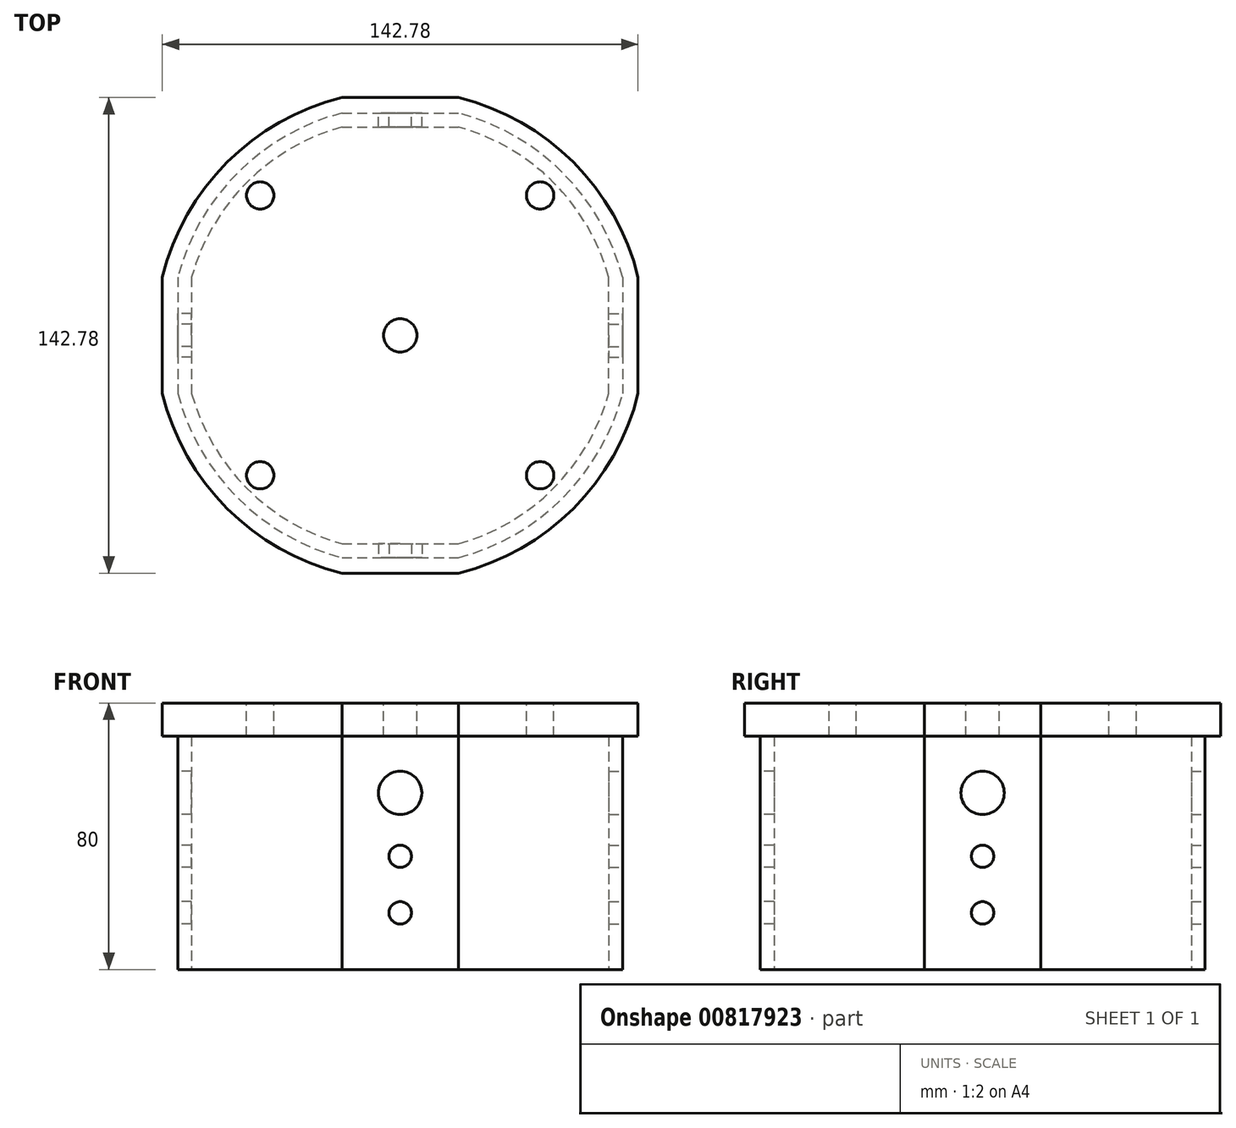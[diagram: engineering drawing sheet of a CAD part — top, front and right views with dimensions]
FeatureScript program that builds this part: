
annotation { "Feature Type Name" : "Feature", "Feature Type Description" : "" }
export const myFeature = defineFeature(function(context is Context, id is Id, definition is map)
    precondition{}
    {
        {
            var Q0;
            Q0=qCreatedBy(makeId("Top.planeOp"),FACE);
            var sketch = newSketch(context, id + "F0", { "sketchPlane" : qUnion([Q0])});
            skArc(sketch, "E0", {"start": v(-17.5, 66.74) * mm, "mid": v(-48.8, 48.8) * mm, "end": v(-66.74, 17.5) * mm});
            skArc(sketch, "E1", {"start": v(-66.74, -17.5) * mm, "mid": v(-48.8, -48.8) * mm, "end": v(-17.5, -66.74) * mm});
            skArc(sketch, "E2", {"start": v(17.5, -66.74) * mm, "mid": v(48.8, -48.8) * mm, "end": v(66.74, -17.5) * mm});
            skArc(sketch, "E3", {"start": v(66.74, 17.5) * mm, "mid": v(48.8, 48.8) * mm, "end": v(17.5, 66.74) * mm});
            skLineSegment(sketch, "E4", {"start": v(-66.74, 17.5) * mm, "end": v(-66.74, -17.5) * mm});
            skLineSegment(sketch, "E5", {"start": v(-17.5, 66.74) * mm, "end": v(17.5, 66.74) * mm});
            skLineSegment(sketch, "E6", {"start": v(66.74, 17.5) * mm, "end": v(66.74, -17.5) * mm});
            skLineSegment(sketch, "E7", {"start": v(-17.5, -66.74) * mm, "end": v(17.5, -66.74) * mm});
            skArc(sketch, "E8", {"start": v(-17.5, 62.6) * mm, "mid": v(-45.96, 45.96) * mm, "end": v(-62.6, 17.5) * mm});
            skArc(sketch, "E9", {"start": v(-62.6, -17.5) * mm, "mid": v(-45.96, -45.96) * mm, "end": v(-17.5, -62.6) * mm});
            skArc(sketch, "E10", {"start": v(17.5, -62.6) * mm, "mid": v(45.96, -45.96) * mm, "end": v(62.6, -17.5) * mm});
            skArc(sketch, "E11", {"start": v(62.6, 17.5) * mm, "mid": v(45.96, 45.96) * mm, "end": v(17.5, 62.6) * mm});
            skLineSegment(sketch, "E12", {"start": v(-17.5, 62.6) * mm, "end": v(17.5, 62.6) * mm});
            skLineSegment(sketch, "E13", {"start": v(-62.6, 17.5) * mm, "end": v(-62.6, -17.5) * mm});
            skLineSegment(sketch, "E14", {"start": v(-17.5, -62.6) * mm, "end": v(17.5, -62.6) * mm});
            skLineSegment(sketch, "E15", {"start": v(62.6, -17.5) * mm, "end": v(62.6, 17.5) * mm});
            skSolve(sketch);
        }
        {
            var Q0;
            Q0 = qSketchRegion(id + "F0", true);
            extrude(context, id + "F1", {"entities" : qUnion([Q0]), "depth" : 70 * mm, "offsetDistance" : 25 * mm});
        }
        {
            var Q0;
            Q0=makeQuery(id+"F1.opExtrude","CAP_FACE",FACE,{"disambiguationData":[OSD([sQuery(id+"F0.wireOp",EDGE,"E0"),sQuery(id+"F0.wireOp",EDGE,"E1"),sQuery(id+"F0.wireOp",EDGE,"E2"),sQuery(id+"F0.wireOp",EDGE,"E3"),sQuery(id+"F0.wireOp",EDGE,"E4"),sQuery(id+"F0.wireOp",EDGE,"E5"),sQuery(id+"F0.wireOp",EDGE,"E6"),sQuery(id+"F0.wireOp",EDGE,"E7"),sQuery(id+"F0.wireOp",EDGE,"E8"),sQuery(id+"F0.wireOp",EDGE,"E9"),sQuery(id+"F0.wireOp",EDGE,"E10"),sQuery(id+"F0.wireOp",EDGE,"E11"),sQuery(id+"F0.wireOp",EDGE,"E12"),sQuery(id+"F0.wireOp",EDGE,"E13"),sQuery(id+"F0.wireOp",EDGE,"E14"),sQuery(id+"F0.wireOp",EDGE,"E15")])],"isStart":false});
            var sketch = newSketch(context, id + "F2", { "sketchPlane" : qUnion([Q0])});
            skArc(sketch, "E16", {"start": v(-17.5, 71.39) * mm, "mid": v(-51.97, 51.97) * mm, "end": v(-71.39, 17.5) * mm});
            skArc(sketch, "E17", {"start": v(-71.39, -17.5) * mm, "mid": v(-51.97, -51.97) * mm, "end": v(-17.5, -71.39) * mm});
            skArc(sketch, "E18", {"start": v(17.5, -71.39) * mm, "mid": v(51.97, -51.97) * mm, "end": v(71.39, -17.5) * mm});
            skArc(sketch, "E19", {"start": v(71.39, 17.5) * mm, "mid": v(51.97, 51.97) * mm, "end": v(17.5, 71.39) * mm});
            skLineSegment(sketch, "E20", {"start": v(-71.39, 17.5) * mm, "end": v(-71.39, -17.5) * mm});
            skLineSegment(sketch, "E21", {"start": v(-17.5, 71.39) * mm, "end": v(17.5, 71.39) * mm});
            skLineSegment(sketch, "E22", {"start": v(71.39, 17.5) * mm, "end": v(71.39, -17.5) * mm});
            skLineSegment(sketch, "E23", {"start": v(-17.5, -71.39) * mm, "end": v(17.5, -71.39) * mm});
            skSolve(sketch);
        }
        {
            var Q0;
            Q0 = qSketchRegion(id + "F2", true);
            extrude(context, id + "F3", {"entities" : qUnion([Q0]), "operationType" : NewBodyOperationType.ADD, "depth" : 10 * mm, "offsetDistance" : 25 * mm});
        }
        {
            var Q0;
            Q0=makeQuery(id+"F1.opExtrude","SWEPT_FACE",FACE,{"disambiguationData":[OSD([sQuery(id+"F0.wireOp",EDGE,"E7")])]});
            var sketch = newSketch(context, id + "F4", { "sketchPlane" : qUnion([Q0])});
            skCircle(sketch, "E24", {"center": v(0, 53) * mm, "radius": 6.5 * mm});
            skCircle(sketch, "E25", {"center": v(0, 34) * mm, "radius": 3.35 * mm});
            skCircle(sketch, "E26", {"center": v(0, 17) * mm, "radius": 3.35 * mm});
            skSolve(sketch);
        }
        {
            var Q0;
            Q0 = qSketchRegion(id + "F4", true);
            extrude(context, id + "F5", {"entities" : qUnion([Q0]), "operationType" : NewBodyOperationType.REMOVE, "endBound" : BoundingType.UP_TO_NEXT, "oppositeDirection" : true, "depth" : 25 * mm, "offsetDistance" : 25 * mm});
        }
        {
            var Q0;
            Q0=makeQuery(id+"F1.opExtrude","SWEPT_FACE",FACE,{"disambiguationData":[OSD([sQuery(id+"F0.wireOp",EDGE,"E6")])]});
            var sketch = newSketch(context, id + "F6", { "sketchPlane" : qUnion([Q0])});
            skCircle(sketch, "E27", {"center": v(0, 53) * mm, "radius": 6.5 * mm});
            skCircle(sketch, "E28", {"center": v(0, 34) * mm, "radius": 3.35 * mm});
            skCircle(sketch, "E29", {"center": v(0, 17) * mm, "radius": 3.35 * mm});
            skSolve(sketch);
        }
        {
            var Q0;
            Q0 = qSketchRegion(id + "F6", true);
            extrude(context, id + "F7", {"entities" : qUnion([Q0]), "operationType" : NewBodyOperationType.REMOVE, "endBound" : BoundingType.UP_TO_NEXT, "oppositeDirection" : true, "depth" : 25 * mm, "offsetDistance" : 25 * mm});
        }
        {
            var Q0;
            Q0=makeQuery(id+"F1.opExtrude","SWEPT_FACE",FACE,{"disambiguationData":[OSD([sQuery(id+"F0.wireOp",EDGE,"E5")])]});
            var sketch = newSketch(context, id + "F8", { "sketchPlane" : qUnion([Q0])});
            skCircle(sketch, "E30", {"center": v(0, 53) * mm, "radius": 6.5 * mm});
            skCircle(sketch, "E31", {"center": v(0, 34) * mm, "radius": 3.35 * mm});
            skCircle(sketch, "E32", {"center": v(0, 17) * mm, "radius": 3.35 * mm});
            skSolve(sketch);
        }
        {
            var Q0;
            Q0 = qSketchRegion(id + "F8", true);
            extrude(context, id + "F9", {"entities" : qUnion([Q0]), "operationType" : NewBodyOperationType.REMOVE, "endBound" : BoundingType.UP_TO_NEXT, "oppositeDirection" : true, "depth" : 25 * mm, "offsetDistance" : 25 * mm});
        }
        {
            var Q0;
            Q0=makeQuery(id+"F1.opExtrude","SWEPT_FACE",FACE,{"disambiguationData":[OSD([sQuery(id+"F0.wireOp",EDGE,"E4")])]});
            var sketch = newSketch(context, id + "F10", { "sketchPlane" : qUnion([Q0])});
            skCircle(sketch, "E33", {"center": v(0, 53) * mm, "radius": 6.5 * mm});
            skCircle(sketch, "E34", {"center": v(0, 34) * mm, "radius": 3.35 * mm});
            skCircle(sketch, "E35", {"center": v(0, 17) * mm, "radius": 3.35 * mm});
            skSolve(sketch);
        }
        {
            var Q0;
            Q0 = qSketchRegion(id + "F10", true);
            extrude(context, id + "F11", {"entities" : qUnion([Q0]), "operationType" : NewBodyOperationType.REMOVE, "endBound" : BoundingType.UP_TO_NEXT, "oppositeDirection" : true, "depth" : 25 * mm, "offsetDistance" : 25 * mm});
        }
        {
            var Q0;
            Q0=makeQuery(id+"F3.opExtrude","CAP_FACE",FACE,{"disambiguationData":[OSD([sQuery(id+"F2.wireOp",EDGE,"E16"),sQuery(id+"F2.wireOp",EDGE,"E17"),sQuery(id+"F2.wireOp",EDGE,"E18"),sQuery(id+"F2.wireOp",EDGE,"E19"),sQuery(id+"F2.wireOp",EDGE,"E20"),sQuery(id+"F2.wireOp",EDGE,"E21"),sQuery(id+"F2.wireOp",EDGE,"E22"),sQuery(id+"F2.wireOp",EDGE,"E23")])],"isStart":false});
            var sketch = newSketch(context, id + "F12", { "sketchPlane" : qUnion([Q0])});
            skCircle(sketch, "E36", {"center": v(0, 0) * mm, "radius": 5 * mm});
            skCircle(sketch, "E37", {"center": v(-42, 42) * mm, "radius": 4.1 * mm});
            skCircle(sketch, "E38", {"center": v(42, 42) * mm, "radius": 4.1 * mm});
            skCircle(sketch, "E39", {"center": v(42, -42) * mm, "radius": 4.1 * mm});
            skCircle(sketch, "E40", {"center": v(-42, -42) * mm, "radius": 4.1 * mm});
            skSolve(sketch);
        }
        {
            var Q0;
            Q0 = qSketchRegion(id + "F12", true);
            var Q1;
            Q1=makeQuery(id+"F3.boolean.opBoolean","SPLIT",FACE,{"disambiguationData":[TD([makeQuery(id+"F1.opExtrude","SWEPT_FACE",FACE,{"disambiguationData":[OSD([sQuery(id+"F0.wireOp",EDGE,"E8")])]})])],"derivedFrom":makeQuery(id+"F3.opExtrude","CAP_FACE",FACE,{"disambiguationData":[OSD([sQuery(id+"F2.wireOp",EDGE,"E16"),sQuery(id+"F2.wireOp",EDGE,"E17"),sQuery(id+"F2.wireOp",EDGE,"E18"),sQuery(id+"F2.wireOp",EDGE,"E19"),sQuery(id+"F2.wireOp",EDGE,"E20"),sQuery(id+"F2.wireOp",EDGE,"E21"),sQuery(id+"F2.wireOp",EDGE,"E22"),sQuery(id+"F2.wireOp",EDGE,"E23")])],"isStart":true})});
            extrude(context, id + "F13", {"entities" : qUnion([Q0]), "operationType" : NewBodyOperationType.REMOVE, "endBound" : BoundingType.UP_TO_SURFACE, "oppositeDirection" : true, "depth" : 25 * mm, "endBoundEntityFace" : qUnion([Q1]), "offsetDistance" : 25 * mm});
        }
    });
